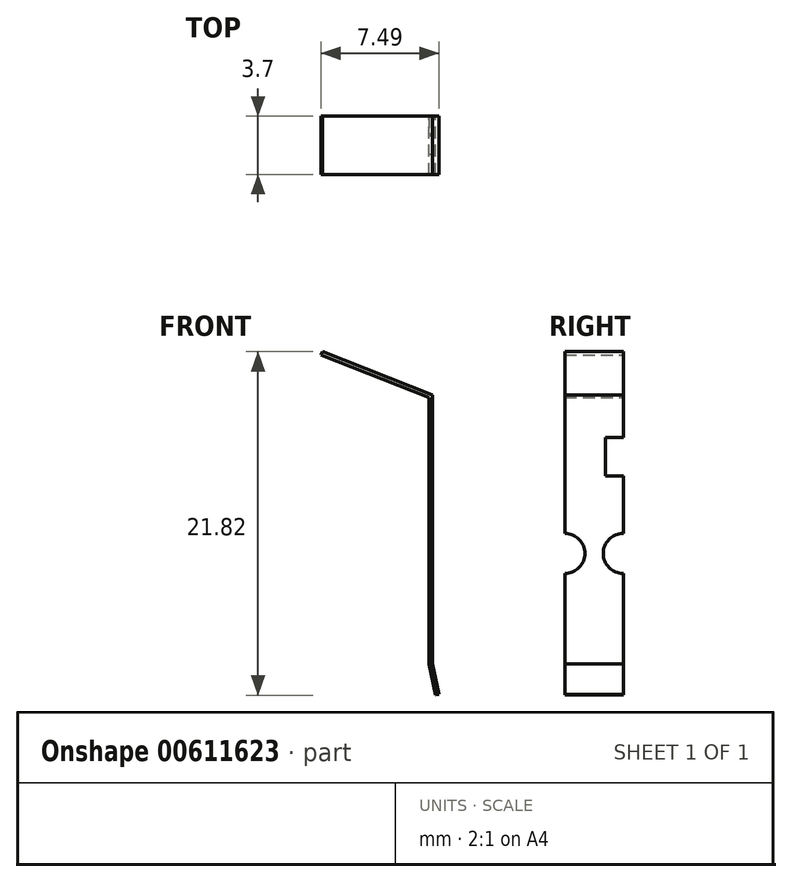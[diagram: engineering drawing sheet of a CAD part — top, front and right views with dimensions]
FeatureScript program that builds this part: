
annotation { "Feature Type Name" : "Feature", "Feature Type Description" : "" }
export const myFeature = defineFeature(function(context is Context, id is Id, definition is map)
    precondition{}
    {
        {
            var Q0;
            Q0=qCreatedBy(makeId("Front.planeOp"),FACE);
            var sketch = newSketch(context, id + "F0", { "sketchPlane" : qUnion([Q0])});
            skLineSegment(sketch, "E0.left", {"start": v(-0.11, 0) * mm, "end": v(-0.11, -16.92) * mm});
            skLineSegment(sketch, "E0.right", {"start": v(0.11, 0) * mm, "end": v(0.11, -16.92) * mm});
            skLineSegment(sketch, "E1", {"start": v(-0.11, -16.92) * mm, "end": v(0.3, -18.9) * mm});
            skLineSegment(sketch, "E2", {"start": v(0.3, -18.9) * mm, "end": v(0.51, -18.86) * mm});
            skLineSegment(sketch, "E3", {"start": v(0.51, -18.86) * mm, "end": v(0.11, -16.92) * mm});
            skLineSegment(sketch, "E4", {"start": v(-0.11, 0) * mm, "end": v(-6.98, 2.7) * mm});
            skLineSegment(sketch, "E5", {"start": v(-6.98, 2.7) * mm, "end": v(-6.9, 2.91) * mm});
            skLineSegment(sketch, "E6", {"start": v(-6.9, 2.91) * mm, "end": v(0.11, 0.16) * mm});
            skLineSegment(sketch, "E7", {"start": v(0.11, 0.16) * mm, "end": v(0.11, 0) * mm});
            skSolve(sketch);
        }
        {
            var Q0;
            Q0=makeQuery(id+"F0.imprint","IMPRINT",FACE,{"disambiguationData":[TD([[makeQuery(id+"F0.imprint","IMPRINT",EDGE,{"derivedFrom":sQuery(id+"F0.wireOp",EDGE,"E0.left")}),1.0]])]});
            extrude(context, id + "F1", {"entities" : qUnion([Q0]), "endBound" : BoundingType.SYMMETRIC, "depth" : 3.7 * mm, "offsetDistance" : 25.4 * mm});
        }
        {
            var Q0;
            Q0=makeQuery(id+"F1.opExtrude","SWEPT_FACE",FACE,{"disambiguationData":[OSD([sQuery(id+"F0.wireOp",EDGE,"E0.left")])]});
            var sketch = newSketch(context, id + "F2", { "sketchPlane" : qUnion([Q0])});
            skLineSegment(sketch, "E8.bottom", {"start": v(-1.85, -2.54) * mm, "end": v(-0.71, -2.54) * mm});
            skLineSegment(sketch, "E8.top", {"start": v(-1.85, -4.98) * mm, "end": v(-0.71, -4.98) * mm});
            skLineSegment(sketch, "E8.left", {"start": v(-1.85, -2.54) * mm, "end": v(-1.85, -4.98) * mm});
            skLineSegment(sketch, "E8.right", {"start": v(-0.71, -2.54) * mm, "end": v(-0.71, -4.98) * mm});
            skCircle(sketch, "E9", {"center": v(-1.85, -9.9) * mm, "radius": 1.27 * mm});
            skCircle(sketch, "E10", {"center": v(1.85, -9.9) * mm, "radius": 1.27 * mm});
            skSolve(sketch);
        }
        {
            var Q0;
            {var subQ0=sQuery(id+"F2.wireOp",EDGE,"E9");var subQ1=makeQuery(id+"F1.opExtrude","CAP_EDGE",EDGE,{"disambiguationData":[OSD([sQuery(id+"F0.wireOp",EDGE,"E0.left")])],"isStart":true});var subQ2=makeQuery(id+"F2.imprint","INTERSECT",VERTEX,{"disambiguationData":[OD(0.0)],"derivedFrom":[subQ1,subQ0]});Q0=makeQuery(id+"F2.imprint","IMPRINT",FACE,{"disambiguationData":[TD([[makeQuery(id+"F2.imprint","IMPRINT",EDGE,{"disambiguationData":[TD([[subQ2,1.0]])],"derivedFrom":subQ0}),1.0]])]});}
            var Q1;
            {var subQ0=sQuery(id+"F2.wireOp",EDGE,"E9");var subQ1=makeQuery(id+"F1.opExtrude","CAP_EDGE",EDGE,{"disambiguationData":[OSD([sQuery(id+"F0.wireOp",EDGE,"E0.left")])],"isStart":true});var subQ2=makeQuery(id+"F2.imprint","INTERSECT",VERTEX,{"disambiguationData":[OD(0.0)],"derivedFrom":[subQ1,subQ0]});Q1=makeQuery(id+"F2.imprint","IMPRINT",FACE,{"disambiguationData":[TD([[makeQuery(id+"F2.imprint","IMPRINT",EDGE,{"disambiguationData":[TD([[subQ2,-1.0]])],"derivedFrom":subQ0}),1.0]])]});}
            var Q2;
            {var subQ0=sQuery(id+"F2.wireOp",EDGE,"E10");var subQ1=makeQuery(id+"F1.opExtrude","CAP_EDGE",EDGE,{"disambiguationData":[OSD([sQuery(id+"F0.wireOp",EDGE,"E0.left")])],"isStart":false});var subQ2=makeQuery(id+"F2.imprint","INTERSECT",VERTEX,{"disambiguationData":[OD(0.0)],"derivedFrom":[subQ1,subQ0]});Q2=makeQuery(id+"F2.imprint","IMPRINT",FACE,{"disambiguationData":[TD([[makeQuery(id+"F2.imprint","IMPRINT",EDGE,{"disambiguationData":[TD([[subQ2,1.0]])],"derivedFrom":subQ0}),1.0]])]});}
            var Q3;
            {var subQ0=sQuery(id+"F2.wireOp",EDGE,"E10");var subQ1=makeQuery(id+"F1.opExtrude","CAP_EDGE",EDGE,{"disambiguationData":[OSD([sQuery(id+"F0.wireOp",EDGE,"E0.left")])],"isStart":false});var subQ2=makeQuery(id+"F2.imprint","INTERSECT",VERTEX,{"disambiguationData":[OD(0.0)],"derivedFrom":[subQ1,subQ0]});Q3=makeQuery(id+"F2.imprint","IMPRINT",FACE,{"disambiguationData":[TD([[makeQuery(id+"F2.imprint","IMPRINT",EDGE,{"disambiguationData":[TD([[subQ2,-1.0]])],"derivedFrom":subQ0}),1.0]])]});}
            var Q4;
            Q4=makeQuery(id+"F2.imprint","IMPRINT",FACE,{"disambiguationData":[TD([[makeQuery(id+"F2.imprint","IMPRINT",EDGE,{"derivedFrom":sQuery(id+"F2.wireOp",EDGE,"E8.bottom")}),-1.0]])]});
            extrude(context, id + "F3", {"entities" : qUnion([Q0, Q1, Q2, Q3, Q4]), "operationType" : NewBodyOperationType.REMOVE, "oppositeDirection" : true, "depth" : 25.4 * mm, "offsetDistance" : 25.4 * mm});
        }
    });
